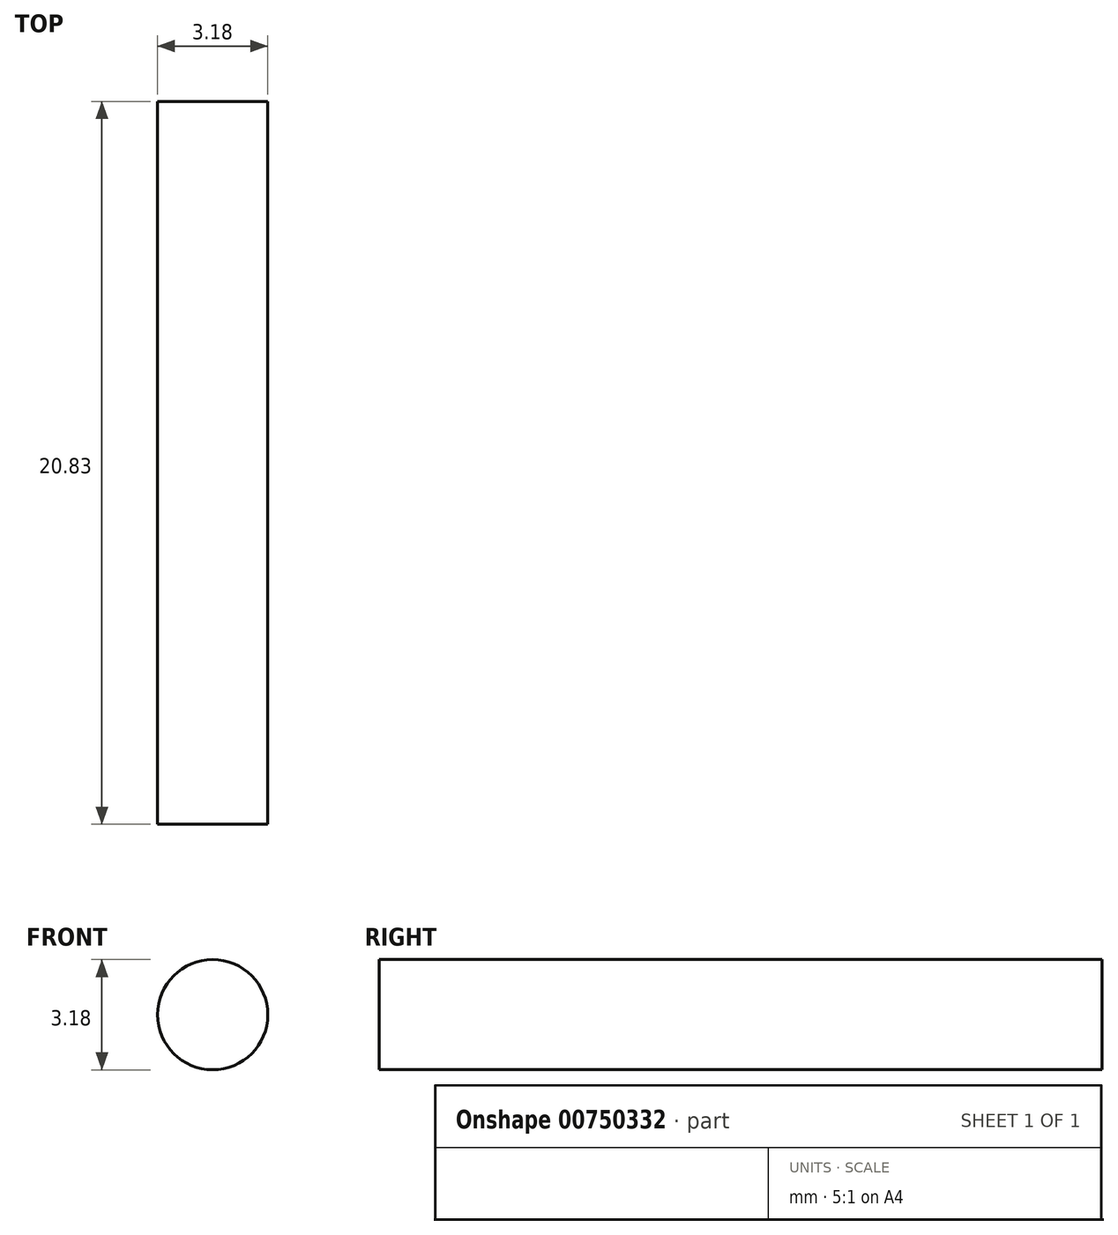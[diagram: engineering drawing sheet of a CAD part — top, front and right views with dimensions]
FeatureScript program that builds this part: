
annotation { "Feature Type Name" : "Feature", "Feature Type Description" : "" }
export const myFeature = defineFeature(function(context is Context, id is Id, definition is map)
    precondition{}
    {
        {
            var Q0;
            Q0=qCreatedBy(makeId("Front.planeOp"),FACE);
            var sketch = newSketch(context, id + "F0", { "sketchPlane" : qUnion([Q0])});
            skCircle(sketch, "E0", {"center": v(0, 0) * mm, "radius": 1.59 * mm});
            skSolve(sketch);
        }
        {
            var Q0;
            Q0 = qSketchRegion(id + "F0", true);
            extrude(context, id + "F1", {"entities" : qUnion([Q0]), "depth" : 20.83 * mm, "offsetDistance" : 25.4 * mm});
        }
    });
